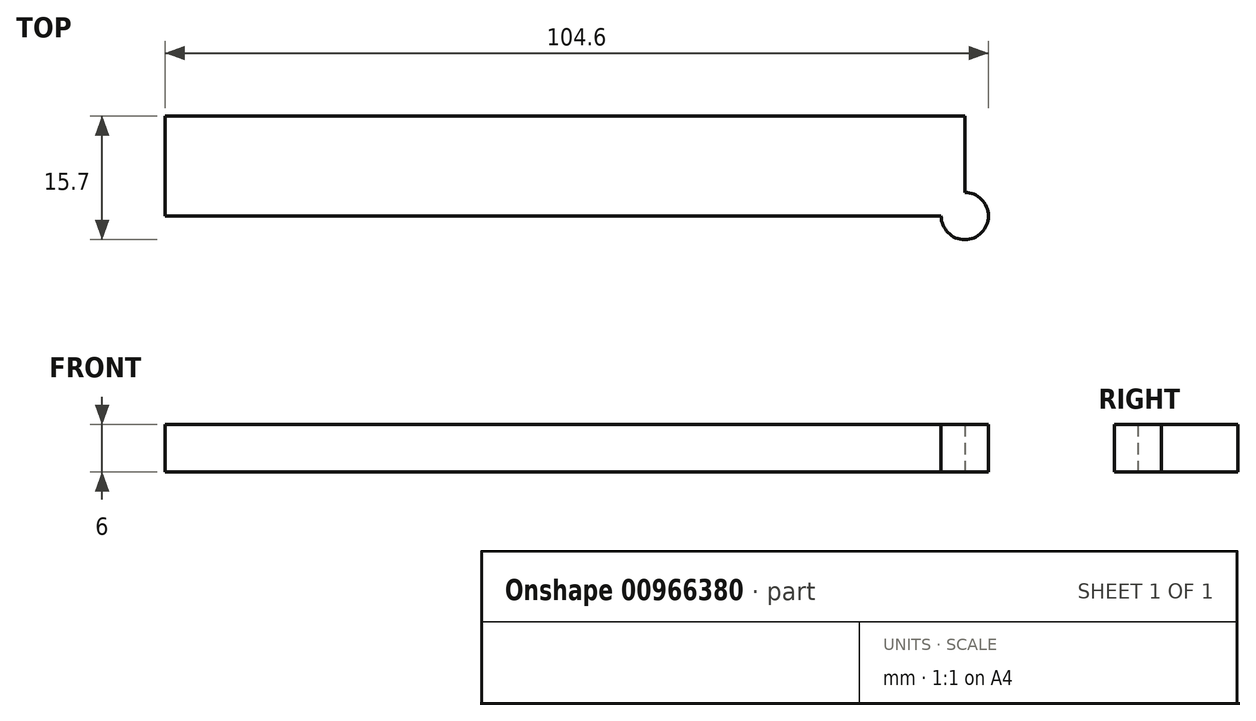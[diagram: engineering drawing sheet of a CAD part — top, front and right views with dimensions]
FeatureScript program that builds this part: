
annotation { "Feature Type Name" : "Feature", "Feature Type Description" : "" }
export const myFeature = defineFeature(function(context is Context, id is Id, definition is map)
    precondition{}
    {
        {
            var Q0;
            Q0=qCreatedBy(makeId("Top.planeOp"),FACE);
            var sketch = newSketch(context, id + "F0", { "sketchPlane" : qUnion([Q0])});
            skLineSegment(sketch, "E0.bottom", {"start": v(0, 0) * mm, "end": v(-101.6, 0) * mm});
            skLineSegment(sketch, "E0.top", {"start": v(0, 12.7) * mm, "end": v(-101.6, 12.7) * mm});
            skLineSegment(sketch, "E0.left", {"start": v(0, 0) * mm, "end": v(0, 12.7) * mm});
            skLineSegment(sketch, "E0.right", {"start": v(-101.6, 0) * mm, "end": v(-101.6, 12.7) * mm});
            skSolve(sketch);
        }
        {
            var Q0;
            Q0=makeQuery(id+"F0.imprint","IMPRINT",FACE,{"disambiguationData":[TD([[makeQuery(id+"F0.imprint","IMPRINT",EDGE,{"derivedFrom":sQuery(id+"F0.wireOp",EDGE,"E0.bottom")}),-1.0]])]});
            extrude(context, id + "F1", {"entities" : qUnion([Q0]), "depth" : 6 * mm, "offsetDistance" : 25.4 * mm});
        }
        {
            var Q0;
            Q0=qCreatedBy(makeId("Top.planeOp"),FACE);
            var sketch = newSketch(context, id + "F2", { "sketchPlane" : qUnion([Q0])});
            skCircle(sketch, "E1", {"center": v(0, 0) * mm, "radius": 3 * mm});
            skSolve(sketch);
        }
        {
            var Q0;
            Q0=makeQuery(id+"F2.imprint","IMPRINT",FACE,{"disambiguationData":[TD([[makeQuery(id+"F2.imprint","IMPRINT",EDGE,{"derivedFrom":sQuery(id+"F2.wireOp",EDGE,"E1")}),1.0]])]});
            extrude(context, id + "F3", {"entities" : qUnion([Q0]), "operationType" : NewBodyOperationType.ADD, "depth" : 6 * mm, "offsetDistance" : 25.4 * mm});
        }
    });
